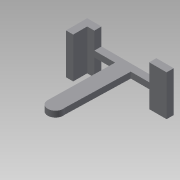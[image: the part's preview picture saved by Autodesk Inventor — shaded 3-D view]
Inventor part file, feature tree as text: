
AUTODESK INVENTOR PART (.ipt)
format: ipt  version: 2015 SP1 (Build 190203100, 203)  size: 255,488 bytes
history: native  units: mm
features: extrude x17, sketch x15, plane x2, projected_geometry x2
ambient origin geometry x8: Origin, YZ Plane, XZ Plane, XY Plane, X Axis, Y Axis, Z Axis, Center Point
bodies: Solid1 (feature_tree)
feature tree (36):
  plane  "Work Plane5"
  sketch  "Sketch4"  dims[d34=15.0mm d36=2.0mm]
  extrude  "Extrusion7"  Depth=2.0mm
  extrude  "Extrusion8"  Depth=17.0mm TaperAngle=0.0deg
  plane  "Work Plane4"
  extrude  "Extrusion9"  Depth=17.0mm
  extrude  "Extrusion10"  Depth=2.0mm
  extrude  "Extrusion11"  Depth=4.0mm TaperAngle=0.0deg
  extrude  "Extrusion12"  Depth=2.0mm TaperAngle=0.0deg
  extrude  "Extrusion13"  Depth=17.0mm TaperAngle=0.0deg
  extrude  "Extrusion14"  Depth=4.0mm TaperAngle=0.0deg
  extrude  "Extrusion15"  Depth=4.0mm TaperAngle=0.0deg
  extrude  "Extrusion16"  Depth=17.0mm TaperAngle=0.0deg
  extrude  "Extrusion18"  Depth=3.0mm
  extrude  "Extrusion19"  Depth=3.0mm TaperAngle=0.0deg
  extrude  "Extrusion20"  Depth=2.0mm
  extrude  "Extrusion21"  Depth=2.0mm TaperAngle=0.0deg
  sketch  "Sketch19"  dims[d78=2.0mm d79=2.0mm d80=0.0mm]
  extrude  "Extrusion22"  Depth=3.0mm TaperAngle=0.0deg
  extrude  "Extrusion23"  [1 undecoded]
  extrude  "Extrusion24"  [1 undecoded]
  sketch  "Sketch5"  dims[d37=2.5mm d38=0.0mm d39=17.0mm d40=0.0mm]
  sketch  "Sketch6"  dims[d41=17.0mm d42=0.0mm d43=2.0mm]
  sketch  "Sketch7"  dims[d44=2.0mm d45=2.0mm]
  sketch  "Sketch8"  dims[d46=2.0mm d47=4.0mm d48=0.0mm]
  sketch  "Sketch9"  dims[d49=5.0mm d50=2.0mm d51=0.0mm]
  sketch  "Sketch10"  dims[d52=2.0mm d53=17.0mm d54=0.0mm]
  sketch  "Sketch12"  dims[d55=2.0mm d56=0.0mm d57=4.0mm d58=0.0mm]
  sketch  "Sketch13"  dims[d59=1.0mm d60=4.0mm d61=0.0mm]
  sketch  "Sketch15"  dims[d62=1.0mm d63=17.0mm d64=0.0mm]
  sketch  "Sketch16"  dims[d68=3.0mm d69=0.0mm d70=3.0mm]
  sketch  "Sketch17"  dims[d71=3.0mm d72=0.0mm d73=2.0mm d74=0.0mm]
  projected_geometry  "Projected Loop2"
  sketch  "Sketch18"  dims[d75=2.0mm d76=0.0mm d77=2.0mm]
  projected_geometry  "Projected Loop3"
  sketch  "Sketch20"  dims[d81=3.0mm d82=0.0mm d83=3.0mm d84=0.0mm]
note: 2 required parameter values undecoded (feature->parameter linkage not recoverable at this tier; creation-order binding heuristic only, values carry confidence <= 0.55)
